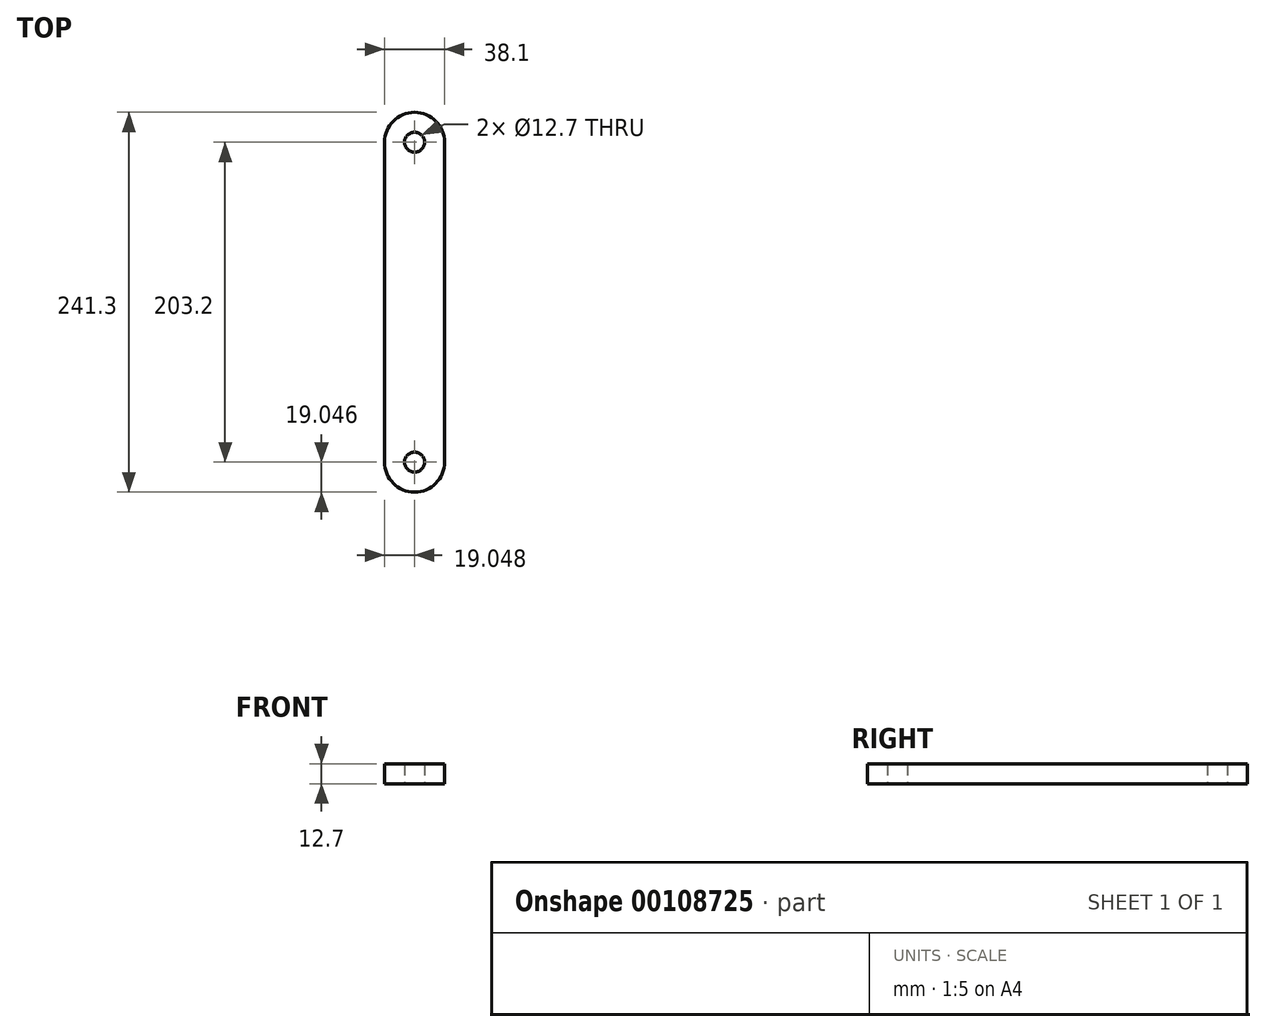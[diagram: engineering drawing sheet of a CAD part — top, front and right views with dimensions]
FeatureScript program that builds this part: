
annotation { "Feature Type Name" : "Feature", "Feature Type Description" : "" }
export const myFeature = defineFeature(function(context is Context, id is Id, definition is map)
    precondition{}
    {
        {
            var Q0;
            Q0=qCreatedBy(makeId("Top.planeOp"),FACE);
            var sketch = newSketch(context, id + "F0", { "sketchPlane" : qUnion([Q0])});
            skLineSegment(sketch, "E0.left", {"start": v(-22.03, -91.04) * mm, "end": v(-22.03, 112.16) * mm});
            skLineSegment(sketch, "E0.right", {"start": v(-60.13, -91.04) * mm, "end": v(-60.13, 112.16) * mm});
            skArc(sketch, "E1", {"start": v(-60.13, 112.16) * mm, "mid": v(-41.08, 131.2) * mm, "end": v(-22.03, 112.16) * mm});
            skArc(sketch, "E2", {"start": v(-60.13, -91.04) * mm, "mid": v(-41.08, -110.1) * mm, "end": v(-22.03, -91.04) * mm});
            skCircle(sketch, "E3", {"center": v(-41.08, 112.16) * mm, "radius": 6.35 * mm});
            skCircle(sketch, "E4", {"center": v(-41.08, -91.04) * mm, "radius": 6.35 * mm});
            skPoint(sketch, "E5.end.orphan", {"position": v(-22.03, 10.56) * mm});
            skPoint(sketch, "E5.start.orphan", {"position": v(-60.13, 10.56) * mm});
            skSolve(sketch);
        }
        {
            var Q0;
            Q0=makeQuery(id+"F0.imprint","IMPRINT",FACE,{"disambiguationData":[TD([[makeQuery(id+"F0.imprint","IMPRINT",EDGE,{"derivedFrom":sQuery(id+"F0.wireOp",EDGE,"E0.left")}),1.0]])]});
            extrude(context, id + "F1", {"entities" : qUnion([Q0]), "depth" : 12.7 * mm});
        }
    });
